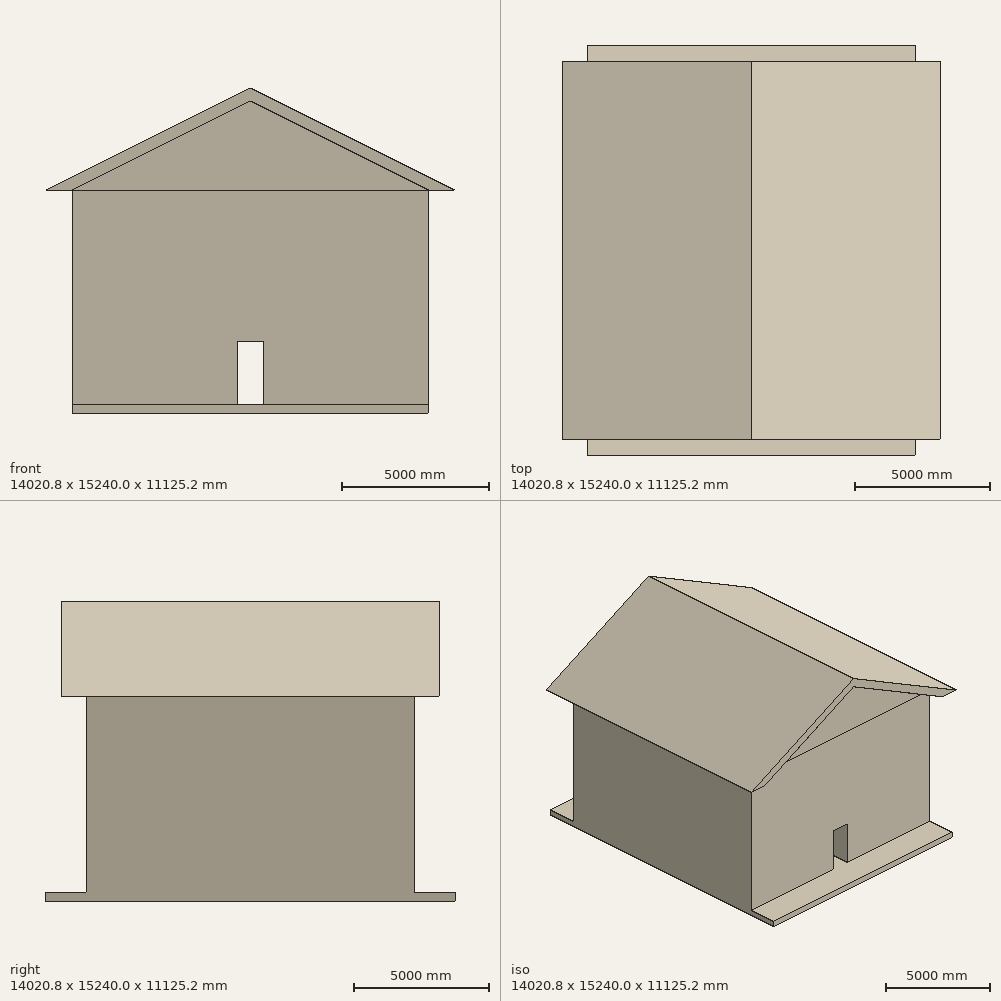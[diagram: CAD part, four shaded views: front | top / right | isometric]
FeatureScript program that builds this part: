
annotation { "Feature Type Name" : "Feature", "Feature Type Description" : "" }
export const myFeature = defineFeature(function(context is Context, id is Id, definition is map)
    precondition{}
    {
        {
            var Q0;
            Q0=qCreatedBy(makeId("Front.planeOp"),FACE);
            var sketch = newSketch(context, id + "F0", { "sketchPlane" : qUnion([Q0])});
            skLineSegment(sketch, "E0", {"start": v(0, 0) * mm, "end": v(-6096, 0) * mm});
            skLineSegment(sketch, "E1", {"start": v(0, 0) * mm, "end": v(6096, 0) * mm});
            skLineSegment(sketch, "E2", {"start": v(0, 0) * mm, "end": v(0, 3048) * mm});
            skLineSegment(sketch, "E3", {"start": v(-6096, 0) * mm, "end": v(0, 3048) * mm});
            skLineSegment(sketch, "E4", {"start": v(6096, 0) * mm, "end": v(0, 3048) * mm});
            skLineSegment(sketch, "E5", {"start": v(-6096, 0) * mm, "end": v(-7010.4, 0) * mm});
            skLineSegment(sketch, "E6", {"start": v(6096, 0) * mm, "end": v(7010.4, 0) * mm});
            skLineSegment(sketch, "E7", {"start": v(0, 3048) * mm, "end": v(0, 3505.2) * mm});
            skLineSegment(sketch, "E8", {"start": v(0, 3505.2) * mm, "end": v(-7010.4, 0) * mm});
            skLineSegment(sketch, "E9", {"start": v(0, 3505.2) * mm, "end": v(7010.4, 0) * mm});
            skLineSegment(sketch, "E10", {"start": v(-6096, 0) * mm, "end": v(-6096, -7315.2) * mm});
            skLineSegment(sketch, "E11", {"start": v(6096, 0) * mm, "end": v(6096, -7315.2) * mm});
            skLineSegment(sketch, "E12", {"start": v(-6096, -7315.2) * mm, "end": v(6096, -7315.2) * mm});
            skLineSegment(sketch, "E13", {"start": v(-6096, -7315.2) * mm, "end": v(-6096, -7620) * mm});
            skLineSegment(sketch, "E14", {"start": v(6096, -7315.2) * mm, "end": v(6096, -7620) * mm});
            skLineSegment(sketch, "E15", {"start": v(-6096, -7620) * mm, "end": v(6096, -7620) * mm});
            skLineSegment(sketch, "E16", {"start": v(0, -7315.2) * mm, "end": v(-457.2, -7315.2) * mm});
            skLineSegment(sketch, "E17", {"start": v(-457.2, -7315.2) * mm, "end": v(-457.2, -5181.6) * mm});
            skLineSegment(sketch, "E18", {"start": v(-457.2, -5181.6) * mm, "end": v(457.2, -5181.6) * mm});
            skLineSegment(sketch, "E19", {"start": v(0, -7315.2) * mm, "end": v(457.2, -7315.2) * mm});
            skLineSegment(sketch, "E20", {"start": v(457.2, -7315.2) * mm, "end": v(457.2, -5181.6) * mm});
            skSolve(sketch);
        }
        {
            var Q0;
            Q0=makeQuery(id+"F0.imprint","IMPRINT",FACE,{"disambiguationData":[TD([[makeQuery(id+"F0.imprint","IMPRINT",EDGE,{"derivedFrom":sQuery(id+"F0.wireOp",EDGE,"E3")}),1.0]])]});
            var Q1;
            Q1=makeQuery(id+"F0.imprint","IMPRINT",FACE,{"disambiguationData":[TD([[makeQuery(id+"F0.imprint","IMPRINT",EDGE,{"derivedFrom":sQuery(id+"F0.wireOp",EDGE,"E4")}),-1.0]])]});
            extrude(context, id + "F1", {"entities" : qUnion([Q0, Q1]), "endBound" : BoundingType.SYMMETRIC, "depth" : 14020.8 * mm, "offsetDistance" : 30.48 * mm});
        }
        {
            var Q0;
            Q0=makeQuery(id+"F0.imprint","IMPRINT",FACE,{"disambiguationData":[TD([[makeQuery(id+"F0.imprint","IMPRINT",EDGE,{"derivedFrom":sQuery(id+"F0.wireOp",EDGE,"E0")}),1.0]])]});
            extrude(context, id + "F2", {"entities" : qUnion([Q0]), "endBound" : BoundingType.SYMMETRIC, "depth" : 12192 * mm, "offsetDistance" : 30.48 * mm});
        }
        {
            var Q0;
            Q0=makeQuery(id+"F0.imprint","IMPRINT",FACE,{"disambiguationData":[TD([[makeQuery(id+"F0.imprint","IMPRINT",EDGE,{"derivedFrom":sQuery(id+"F0.wireOp",EDGE,"E1")}),1.0]])]});
            var Q1;
            Q1=makeQuery(id+"F0.imprint","IMPRINT",FACE,{"disambiguationData":[TD([[makeQuery(id+"F0.imprint","IMPRINT",EDGE,{"derivedFrom":sQuery(id+"F0.wireOp",EDGE,"E0")}),-1.0]])]});
            extrude(context, id + "F3", {"entities" : qUnion([Q0, Q1]), "endBound" : BoundingType.SYMMETRIC, "depth" : 12192 * mm, "offsetDistance" : 30.48 * mm});
        }
        {
            var Q0;
            {var subQ1=sQuery(id+"F0.wireOp",EDGE,"E13");Q0=makeQuery(id+"F0.imprint","IMPRINT",FACE,{"disambiguationData":[TD([[makeQuery(id+"F0.imprint","IMPRINT",EDGE,{"derivedFrom":subQ1}),1.0]])]});}
            extrude(context, id + "F4", {"entities" : qUnion([Q0]), "operationType" : NewBodyOperationType.ADD, "endBound" : BoundingType.SYMMETRIC, "depth" : 15240 * mm, "offsetDistance" : 30.48 * mm});
        }
    });
